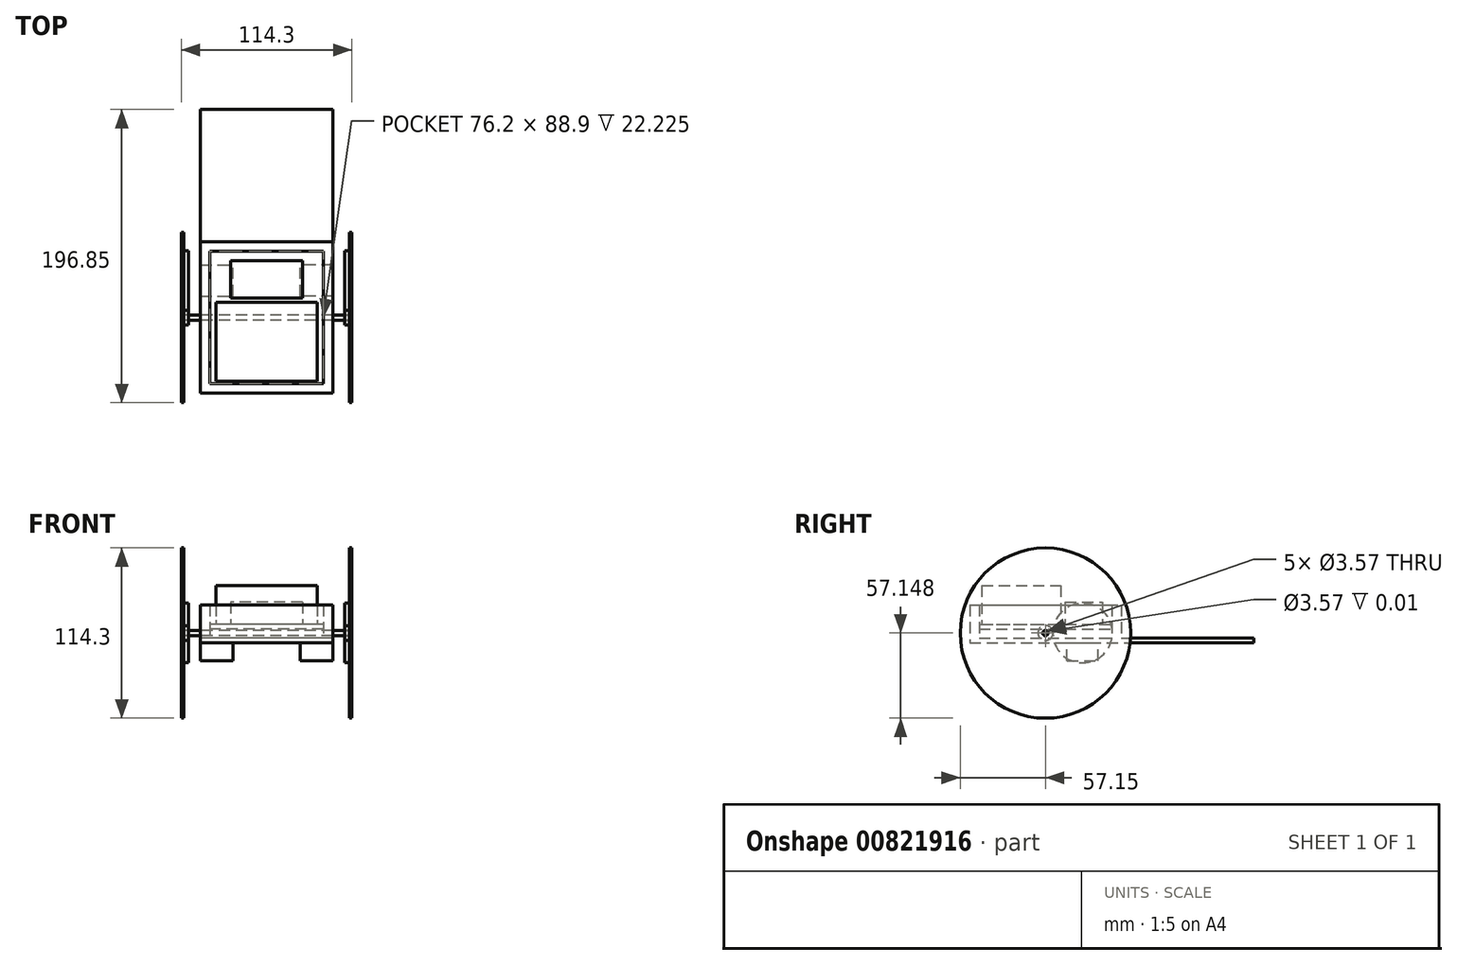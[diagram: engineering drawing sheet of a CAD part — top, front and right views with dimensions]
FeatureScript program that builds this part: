
annotation { "Feature Type Name" : "Feature", "Feature Type Description" : "" }
export const myFeature = defineFeature(function(context is Context, id is Id, definition is map)
    precondition{}
    {
        {
            var Q0;
            Q0=qCreatedBy(makeId("Top.planeOp"),FACE);
            var sketch = newSketch(context, id + "F0", { "sketchPlane" : qUnion([Q0])});
            skLineSegment(sketch, "E0.bottom", {"start": v(44.45, -50.8) * mm, "end": v(-44.45, -50.8) * mm});
            skLineSegment(sketch, "E0.top", {"start": v(44.45, 50.8) * mm, "end": v(-44.45, 50.8) * mm});
            skLineSegment(sketch, "E0.left", {"start": v(44.45, -50.8) * mm, "end": v(44.45, 50.8) * mm});
            skLineSegment(sketch, "E0.right", {"start": v(-44.45, -50.8) * mm, "end": v(-44.45, 50.8) * mm});
            skPoint(sketch, "E0.middle", {"position": v(0, 0) * mm});
            skLineSegment(sketch, "E1.bottom", {"start": v(38.1, -44.45) * mm, "end": v(-38.1, -44.45) * mm});
            skLineSegment(sketch, "E1.top", {"start": v(38.1, 44.45) * mm, "end": v(-38.1, 44.45) * mm});
            skLineSegment(sketch, "E1.left", {"start": v(38.1, -44.45) * mm, "end": v(38.1, 44.45) * mm});
            skLineSegment(sketch, "E1.right", {"start": v(-38.1, -44.45) * mm, "end": v(-38.1, 44.45) * mm});
            skLineSegment(sketch, "E2.top", {"start": v(-44.45, 139.7) * mm, "end": v(44.45, 139.7) * mm});
            skLineSegment(sketch, "E2.left", {"start": v(-44.45, 50.8) * mm, "end": v(-44.45, 139.7) * mm});
            skLineSegment(sketch, "E2.right", {"start": v(44.45, 50.8) * mm, "end": v(44.45, 139.7) * mm});
            skSolve(sketch);
        }
        {
            var Q0;
            Q0=makeQuery(id+"F0.imprint","IMPRINT",FACE,{"disambiguationData":[TD([[makeQuery(id+"F0.imprint","IMPRINT",EDGE,{"derivedFrom":sQuery(id+"F0.wireOp",EDGE,"E0.bottom")}),-1.0]])]});
            extrude(context, id + "F1", {"entities" : qUnion([Q0]), "depth" : 25.4 * mm, "offsetDistance" : 25.4 * mm});
        }
        {
            var Q0;
            Q0=makeQuery(id+"F0.imprint","IMPRINT",FACE,{"disambiguationData":[TD([[makeQuery(id+"F0.imprint","IMPRINT",EDGE,{"derivedFrom":sQuery(id+"F0.wireOp",EDGE,"E1.bottom")}),-1.0]])]});
            extrude(context, id + "F2", {"entities" : qUnion([Q0]), "operationType" : NewBodyOperationType.ADD, "depth" : 3.17 * mm, "offsetDistance" : 25.4 * mm});
        }
        {
            var Q0;
            Q0=makeQuery(id+"F1.opExtrude","SWEPT_FACE",FACE,{"disambiguationData":[OSD([sQuery(id+"F0.wireOp",EDGE,"E1.right")])]});
            var sketch = newSketch(context, id + "F3", { "sketchPlane" : qUnion([Q0])});
            skLineSegment(sketch, "E3.bottom", {"start": v(-44.45, 12.3) * mm, "end": v(44.45, 12.3) * mm});
            skLineSegment(sketch, "E3.top", {"start": v(-44.45, 9.13) * mm, "end": v(44.45, 9.13) * mm});
            skLineSegment(sketch, "E3.left", {"start": v(-44.45, 12.3) * mm, "end": v(-44.45, 9.13) * mm});
            skLineSegment(sketch, "E3.right", {"start": v(44.45, 12.3) * mm, "end": v(44.45, 9.13) * mm});
            skSolve(sketch);
        }
        {
            var Q0;
            Q0=makeQuery(id+"F3.imprint","IMPRINT",FACE,{"disambiguationData":[TD([[makeQuery(id+"F3.imprint","IMPRINT",EDGE,{"derivedFrom":sQuery(id+"F3.wireOp",EDGE,"E3.bottom")}),-1.0]])]});
            extrude(context, id + "F4", {"entities" : qUnion([Q0]), "depth" : 76.2 * mm, "offsetDistance" : 25.4 * mm});
        }
        {
            var Q0;
            Q0=makeQuery(id+"F4.opExtrude","SWEPT_FACE",FACE,{"disambiguationData":[OSD([sQuery(id+"F3.wireOp",EDGE,"E3.bottom")])]});
            var sketch = newSketch(context, id + "F5", { "sketchPlane" : qUnion([Q0])});
            skLineSegment(sketch, "E4.bottom", {"start": v(24, 13.2) * mm, "end": v(-24, 13.2) * mm});
            skLineSegment(sketch, "E4.top", {"start": v(24, 38.2) * mm, "end": v(-24, 38.2) * mm});
            skLineSegment(sketch, "E4.left", {"start": v(24, 13.2) * mm, "end": v(24, 38.2) * mm});
            skLineSegment(sketch, "E4.right", {"start": v(-24, 13.2) * mm, "end": v(-24, 38.2) * mm});
            skPoint(sketch, "E4.middle", {"position": v(0, 25.7) * mm});
            skLineSegment(sketch, "E5.bottom", {"start": v(34, -42.7) * mm, "end": v(-34, -42.7) * mm});
            skLineSegment(sketch, "E5.top", {"start": v(34, 10.3) * mm, "end": v(-34, 10.3) * mm});
            skLineSegment(sketch, "E5.left", {"start": v(34, -42.7) * mm, "end": v(34, 10.3) * mm});
            skLineSegment(sketch, "E5.right", {"start": v(-34, -42.7) * mm, "end": v(-34, 10.3) * mm});
            skPoint(sketch, "E5.middle", {"position": v(0, -16.2) * mm});
            skSolve(sketch);
        }
        {
            var Q0;
            Q0=makeQuery(id+"F5.imprint","IMPRINT",FACE,{"disambiguationData":[TD([[makeQuery(id+"F5.imprint","IMPRINT",EDGE,{"derivedFrom":sQuery(id+"F5.wireOp",EDGE,"E4.bottom")}),-1.0]])]});
            extrude(context, id + "F6", {"entities" : qUnion([Q0]), "depth" : 15 * mm, "offsetDistance" : 25.4 * mm});
        }
        {
            var Q0;
            {var subQ0=sQuery(id+"F5.wireOp",EDGE,"E5.top");Q0=makeQuery(id+"F5.imprint","IMPRINT",FACE,{"disambiguationData":[TD([[makeQuery(id+"F5.imprint","IMPRINT",EDGE,{"derivedFrom":subQ0}),1.0]])]});}
            extrude(context, id + "F7", {"entities" : qUnion([Q0]), "depth" : 26 * mm, "offsetDistance" : 25.4 * mm});
        }
        {
            var Q0;
            Q0=makeQuery(id+"F1.opExtrude","SWEPT_FACE",FACE,{"disambiguationData":[OSD([sQuery(id+"F0.wireOp",EDGE,"E0.right")])]});
            var sketch = newSketch(context, id + "F8", { "sketchPlane" : qUnion([Q0])});
            skLineSegment(sketch, "E6", {"start": v(0, 0) * mm, "end": v(0, 25.4) * mm, "construction": true});
            skCircle(sketch, "E7", {"center": v(0, 6.55) * mm, "radius": 1.79 * mm});
            skSolve(sketch);
        }
        {
            var Q0;
            Q0=makeQuery(id+"F8.imprint","IMPRINT",FACE,{"disambiguationData":[TD([[makeQuery(id+"F8.imprint","IMPRINT",EDGE,{"derivedFrom":sQuery(id+"F8.wireOp",EDGE,"E7")}),1.0]])]});
            extrude(context, id + "F9", {"entities" : qUnion([Q0]), "operationType" : NewBodyOperationType.REMOVE, "oppositeDirection" : true, "depth" : 6.35 * mm, "offsetDistance" : 25.4 * mm});
        }
        {
            var Q0;
            Q0=makeQuery(id+"F1.opExtrude","SWEPT_FACE",FACE,{"disambiguationData":[OSD([sQuery(id+"F0.wireOp",EDGE,"E0.left")])]});
            var sketch = newSketch(context, id + "F10", { "sketchPlane" : qUnion([Q0])});
            skLineSegment(sketch, "E8", {"start": v(0, 0) * mm, "end": v(0, 25.4) * mm, "construction": true});
            skCircle(sketch, "E9", {"center": v(0, 6.55) * mm, "radius": 1.79 * mm});
            skSolve(sketch);
        }
        {
            var Q0;
            Q0=makeQuery(id+"F10.imprint","IMPRINT",FACE,{"disambiguationData":[TD([[makeQuery(id+"F10.imprint","IMPRINT",EDGE,{"derivedFrom":sQuery(id+"F10.wireOp",EDGE,"E9")}),1.0]])]});
            extrude(context, id + "F11", {"entities" : qUnion([Q0]), "operationType" : NewBodyOperationType.REMOVE, "oppositeDirection" : true, "depth" : 1 / 101.6 * mm, "offsetDistance" : 25.4 * mm});
        }
        {
            var Q0;
            Q0=makeQuery(id+"F8.imprint","IMPRINT",FACE,{"disambiguationData":[TD([[makeQuery(id+"F8.imprint","IMPRINT",EDGE,{"derivedFrom":sQuery(id+"F8.wireOp",EDGE,"E7")}),1.0]])]});
            extrude(context, id + "F12", {"entities" : qUnion([Q0]), "oppositeDirection" : true, "depth" : 57.15 * mm, "offsetDistance" : 25.4 * mm, "hasSecondDirection" : true, "secondDirectionOppositeDirection" : false, "secondDirectionDepth" : 57.15 * mm});
        }
        {
            var Q0;
            Q0=makeQuery(id+"F12.opExtrude","SWEPT_BODY",BODY,{"disambiguationData":[OSD([sQuery(id+"F8.wireOp",EDGE,"E7")])]});
            transform(context, id + "F13", {"entities" : qUnion([Q0]), "transformType" : TransformType.TRANSLATION_3D, "dx" : 38.1 * mm, "dy" : 0 * mm, "dz" : 0 * mm, "makeCopy" : false});
        }
        {
            var Q0;
            Q0=makeQuery(id+"F12.opExtrude","SWEPT_BODY",BODY,{"disambiguationData":[OSD([sQuery(id+"F8.wireOp",EDGE,"E7")])]});
            transform(context, id + "F14", {"entities" : qUnion([Q0]), "transformType" : TransformType.TRANSLATION_3D, "dx" : 6.35 * mm, "dy" : 0 * mm, "dz" : 0 * mm, "makeCopy" : false});
        }
        {
            var Q0;
            Q0=makeQuery(id+"F12.opExtrude","CAP_FACE",FACE,{"disambiguationData":[OSD([sQuery(id+"F8.wireOp",EDGE,"E7")])],"isStart":false});
            var sketch = newSketch(context, id + "F15", { "sketchPlane" : qUnion([Q0])});
            skCircle(sketch, "E10", {"center": v(0, 6.55) * mm, "radius": 57.15 * mm});
            skSolve(sketch);
        }
        {
            var Q0;
            Q0=makeQuery(id+"F15.imprint","IMPRINT",FACE,{"disambiguationData":[TD([[makeQuery(id+"F15.imprint","IMPRINT",EDGE,{"derivedFrom":sQuery(id+"F15.wireOp",EDGE,"E10")}),1.0]])]});
            extrude(context, id + "F16", {"entities" : qUnion([Q0]), "oppositeDirection" : true, "depth" : 1.59 * mm, "offsetDistance" : 25.4 * mm});
        }
        {
            var Q0;
            Q0=makeQuery(id+"F12.opExtrude","CAP_FACE",FACE,{"disambiguationData":[OSD([sQuery(id+"F8.wireOp",EDGE,"E7")])],"isStart":true});
            var sketch = newSketch(context, id + "F17", { "sketchPlane" : qUnion([Q0])});
            skCircle(sketch, "E11", {"center": v(0, 6.55) * mm, "radius": 57.15 * mm});
            skSolve(sketch);
        }
        {
            var Q0;
            Q0=makeQuery(id+"F17.imprint","IMPRINT",FACE,{"disambiguationData":[TD([[makeQuery(id+"F17.imprint","IMPRINT",EDGE,{"derivedFrom":sQuery(id+"F17.wireOp",EDGE,"E11")}),1.0]])]});
            extrude(context, id + "F18", {"entities" : qUnion([Q0]), "oppositeDirection" : true, "depth" : 1.59 * mm, "offsetDistance" : 25.4 * mm});
        }
        {
            var Q0;
            Q0=makeQuery(id+"F18.opExtrude","CAP_FACE",FACE,{"disambiguationData":[OSD([sQuery(id+"F8.wireOp",EDGE,"E7"),sQuery(id+"F17.wireOp",EDGE,"E11")])],"isStart":false});
            var sketch = newSketch(context, id + "F19", { "sketchPlane" : qUnion([Q0])});
            skSolve(sketch);
        }
        {
            var Q0;
            Q0=makeQuery(id+"F16.opExtrude","CAP_FACE",FACE,{"disambiguationData":[OSD([sQuery(id+"F8.wireOp",EDGE,"E7"),sQuery(id+"F15.wireOp",EDGE,"E10")])],"isStart":false});
            var sketch = newSketch(context, id + "F20", { "sketchPlane" : qUnion([Q0])});
            skCircle(sketch, "E12", {"center": v(0, 6.55) * mm, "radius": 5 * mm});
            skCircle(sketch, "E13", {"center": v(-25, 6.55) * mm, "radius": 20 * mm});
            skSolve(sketch);
        }
        {
            var Q0;
            Q0=makeQuery(id+"F20.imprint","IMPRINT",FACE,{"disambiguationData":[TD([[makeQuery(id+"F20.imprint","IMPRINT",EDGE,{"derivedFrom":sQuery(id+"F20.wireOp",EDGE,"E12")}),1.0]])]});
            extrude(context, id + "F21", {"entities" : qUnion([Q0]), "depth" : 3.17 * mm, "offsetDistance" : 25.4 * mm});
        }
        {
            var Q0;
            Q0=makeQuery(id+"F19.imprint","IMPRINT",FACE,{"disambiguationData":[TD([[makeQuery(id+"F19.imprint","IMPRINT",EDGE,{"derivedFrom":makeQuery(id+"F18.opExtrude","CAP_EDGE",EDGE,{"disambiguationData":[OSD([sQuery(id+"F17.wireOp",EDGE,"E11")])],"isStart":false})}),-1.0]])]});
            var sketch = newSketch(context, id + "F22", { "sketchPlane" : qUnion([Q0])});
            skCircle(sketch, "E14", {"center": v(0, 6.55) * mm, "radius": 5 * mm});
            skCircle(sketch, "E15", {"center": v(25, 6.55) * mm, "radius": 20 * mm});
            skSolve(sketch);
        }
        {
            var Q0;
            Q0=makeQuery(id+"F22.imprint","IMPRINT",FACE,{"disambiguationData":[TD([[makeQuery(id+"F22.imprint","IMPRINT",EDGE,{"derivedFrom":sQuery(id+"F22.wireOp",EDGE,"E14")}),1.0]])]});
            extrude(context, id + "F23", {"entities" : qUnion([Q0]), "depth" : 3.17 * mm, "offsetDistance" : 25.4 * mm});
        }
        {
            var Q0;
            Q0=makeQuery(id+"F20.imprint","IMPRINT",FACE,{"disambiguationData":[TD([[makeQuery(id+"F20.imprint","IMPRINT",EDGE,{"derivedFrom":sQuery(id+"F20.wireOp",EDGE,"E13")}),1.0]])]});
            extrude(context, id + "F24", {"entities" : qUnion([Q0]), "depth" : 3.17 * mm, "offsetDistance" : 25.4 * mm});
        }
        {
            var Q0;
            Q0=makeQuery(id+"F22.imprint","IMPRINT",FACE,{"disambiguationData":[TD([[makeQuery(id+"F22.imprint","IMPRINT",EDGE,{"derivedFrom":sQuery(id+"F22.wireOp",EDGE,"E15")}),1.0]])]});
            extrude(context, id + "F25", {"entities" : qUnion([Q0]), "depth" : 3.17 * mm, "offsetDistance" : 25.4 * mm});
        }
        {
            var Q0;
            Q0=makeQuery(id+"F0.imprint","IMPRINT",FACE,{"disambiguationData":[TD([[makeQuery(id+"F0.imprint","IMPRINT",EDGE,{"derivedFrom":sQuery(id+"F0.wireOp",EDGE,"E0.top")}),-1.0]])]});
            extrude(context, id + "F26", {"entities" : qUnion([Q0]), "operationType" : NewBodyOperationType.ADD, "depth" : 3.17 * mm, "offsetDistance" : 25.4 * mm});
        }
        {
            var Q0;
            {var subQ0=sQuery(id+"F0.wireOp",EDGE,"E0.top");var subQ1=sQuery(id+"F0.wireOp",EDGE,"E1.right");var subQ2=sQuery(id+"F0.wireOp",EDGE,"E1.left");var subQ3=sQuery(id+"F0.wireOp",EDGE,"E1.top");var subQ4=sQuery(id+"F0.wireOp",EDGE,"E1.bottom");Q0=makeQuery(id+"F26.boolean.opBoolean","MERGE",FACE,{"derivedFrom":[makeQuery(id+"F2.boolean.opBoolean","MERGE",FACE,{"derivedFrom":[makeQuery(id+"F1.opExtrude","CAP_FACE",FACE,{"disambiguationData":[OSD([sQuery(id+"F0.wireOp",EDGE,"E0.bottom"),subQ0,sQuery(id+"F0.wireOp",EDGE,"E0.left"),sQuery(id+"F0.wireOp",EDGE,"E0.right"),subQ4,subQ3,subQ2,subQ1])],"isStart":true}),makeQuery(id+"F2.opExtrude","CAP_FACE",FACE,{"disambiguationData":[OSD([subQ4,subQ3,subQ2,subQ1])],"isStart":true})]}),makeQuery(id+"F26.opExtrude","CAP_FACE",FACE,{"disambiguationData":[OSD([subQ0,sQuery(id+"F0.wireOp",EDGE,"E2.top"),sQuery(id+"F0.wireOp",EDGE,"E2.left"),sQuery(id+"F0.wireOp",EDGE,"E2.right")])],"isStart":true})]});}
            var sketch = newSketch(context, id + "F27", { "sketchPlane" : qUnion([Q0])});
            skLineSegment(sketch, "E16.bottom", {"start": v(-44.45, -14.5) * mm, "end": v(-22.45, -14.5) * mm});
            skLineSegment(sketch, "E16.top", {"start": v(-44.45, -35.5) * mm, "end": v(-22.45, -35.5) * mm});
            skLineSegment(sketch, "E16.left", {"start": v(-44.45, -14.5) * mm, "end": v(-44.45, -35.5) * mm});
            skLineSegment(sketch, "E16.right", {"start": v(-22.45, -14.5) * mm, "end": v(-22.45, -35.5) * mm});
            skLineSegment(sketch, "E17.bottom", {"start": v(44.45, -14.5) * mm, "end": v(22.45, -14.5) * mm});
            skLineSegment(sketch, "E17.top", {"start": v(44.45, -35.5) * mm, "end": v(22.45, -35.5) * mm});
            skLineSegment(sketch, "E17.left", {"start": v(44.45, -14.5) * mm, "end": v(44.45, -35.5) * mm});
            skLineSegment(sketch, "E17.right", {"start": v(22.45, -14.5) * mm, "end": v(22.45, -35.5) * mm});
            skPoint(sketch, "E18", {"position": v(44.45, -25) * mm});
            skPoint(sketch, "E19", {"position": v(-44.45, -25) * mm});
            skPoint(sketch, "E20", {"position": v(44.45, 0) * mm});
            skPoint(sketch, "E21", {"position": v(-44.45, 0) * mm});
            skSolve(sketch);
        }
        {
            var Q0;
            Q0=makeQuery(id+"F27.imprint","IMPRINT",FACE,{"disambiguationData":[TD([[makeQuery(id+"F27.imprint","IMPRINT",EDGE,{"derivedFrom":sQuery(id+"F27.wireOp",EDGE,"E16.bottom")}),-1.0]])]});
            var Q1;
            Q1=makeQuery(id+"F27.imprint","IMPRINT",FACE,{"disambiguationData":[TD([[makeQuery(id+"F27.imprint","IMPRINT",EDGE,{"derivedFrom":sQuery(id+"F27.wireOp",EDGE,"E17.bottom")}),1.0]])]});
            extrude(context, id + "F28", {"entities" : qUnion([Q0, Q1]), "depth" : 12 * mm, "offsetDistance" : 25.4 * mm});
        }
    });
